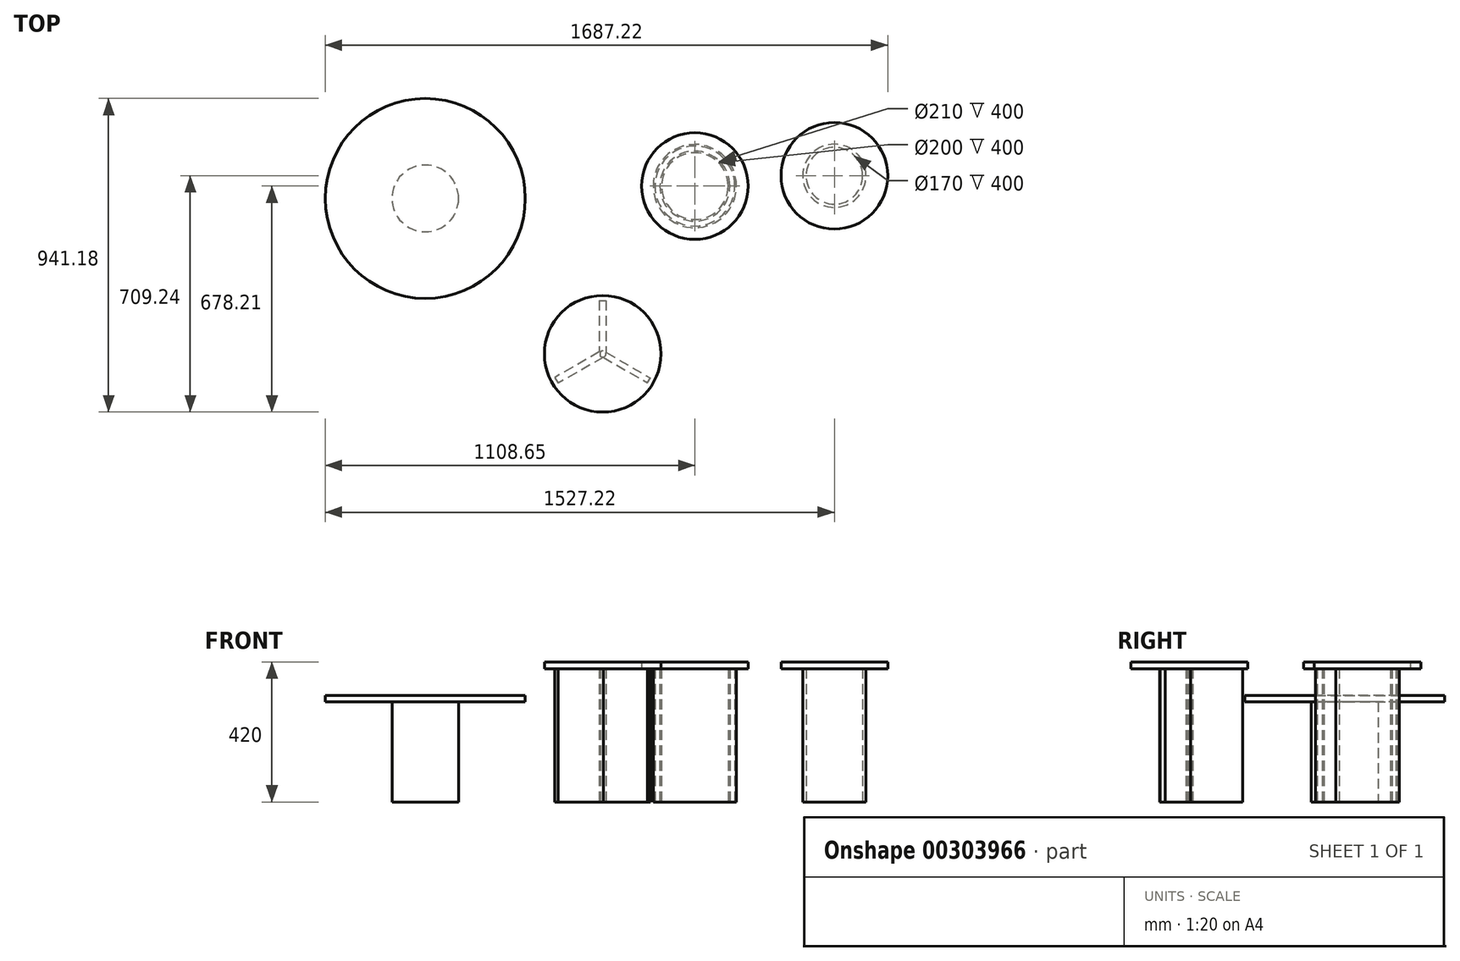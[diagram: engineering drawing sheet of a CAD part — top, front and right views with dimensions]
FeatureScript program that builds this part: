
annotation { "Feature Type Name" : "Feature", "Feature Type Description" : "" }
export const myFeature = defineFeature(function(context is Context, id is Id, definition is map)
    precondition{}
    {
        {
            var Q0;
            Q0=qCreatedBy(makeId("Top.planeOp"),FACE);
            var sketch = newSketch(context, id + "F0", { "sketchPlane" : qUnion([Q0])});
            skCircle(sketch, "E0", {"center": v(0, 0) * mm, "radius": 125 * mm});
            skCircle(sketch, "E1", {"center": v(0, 0) * mm, "radius": 100 * mm});
            skSolve(sketch);
        }
        {
            var Q0;
            Q0 = qSketchRegion(id + "F0", true);
            extrude(context, id + "F1", {"entities" : qUnion([Q0]), "depth" : 400 * mm});
        }
        {
            var Q0;
            Q0=qCreatedBy(makeId("Top.planeOp"),FACE);
            var sketch = newSketch(context, id + "F2", { "sketchPlane" : qUnion([Q0])});
            skCircle(sketch, "E2.0", {"center": v(0, 0) * mm, "radius": 125 * mm, "construction": true});
            skCircle(sketch, "E2.1", {"center": v(0, 0) * mm, "radius": 100 * mm, "construction": true});
            skCircle(sketch, "E3", {"center": v(0, 0) * mm, "radius": 120 * mm});
            skCircle(sketch, "E4", {"center": v(0, 0) * mm, "radius": 105 * mm});
            skSolve(sketch);
        }
        {
            var Q0;
            Q0 = qSketchRegion(id + "F2", true);
            var Q1;
            Q1=makeQuery(id+"F1.opExtrude","CAP_FACE",FACE,{"disambiguationData":[OSD([sQuery(id+"F0.wireOp",EDGE,"E0"),sQuery(id+"F0.wireOp",EDGE,"E1")])],"isStart":false});
            extrude(context, id + "F3", {"entities" : qUnion([Q0]), "endBound" : BoundingType.UP_TO_SURFACE, "endBoundEntityFace" : qUnion([Q1]), "depth" : 25 * mm});
        }
        {
            var Q0;
            Q0=makeQuery(id+"F1.opExtrude","CAP_FACE",FACE,{"disambiguationData":[OSD([sQuery(id+"F0.wireOp",EDGE,"E0"),sQuery(id+"F0.wireOp",EDGE,"E1")])],"isStart":false});
            var sketch = newSketch(context, id + "F4", { "sketchPlane" : qUnion([Q0])});
            skCircle(sketch, "E5", {"center": v(0, 0) * mm, "radius": 160 * mm});
            skSolve(sketch);
        }
        {
            var Q0;
            Q0 = qSketchRegion(id + "F4", true);
            extrude(context, id + "F5", {"entities" : qUnion([Q0]), "depth" : 20 * mm});
        }
        {
            var Q0;
            Q0=qCreatedBy(makeId("Top.planeOp"),FACE);
            var sketch = newSketch(context, id + "F6", { "sketchPlane" : qUnion([Q0])});
            skCircle(sketch, "E6", {"center": v(418.57, 31.03) * mm, "radius": 95 * mm});
            skCircle(sketch, "E7", {"center": v(418.57, 31.03) * mm, "radius": 85 * mm});
            skSolve(sketch);
        }
        {
            var Q0;
            Q0 = qSketchRegion(id + "F6", true);
            extrude(context, id + "F7", {"entities" : qUnion([Q0]), "depth" : 400 * mm});
        }
        {
            var Q0;
            Q0=makeQuery(id+"F7.opExtrude","CAP_FACE",FACE,{"disambiguationData":[OSD([sQuery(id+"F6.wireOp",EDGE,"E6"),sQuery(id+"F6.wireOp",EDGE,"E7")])],"isStart":false});
            var sketch = newSketch(context, id + "F8", { "sketchPlane" : qUnion([Q0])});
            skCircle(sketch, "E8", {"center": v(418.57, 31.03) * mm, "radius": 160 * mm});
            skSolve(sketch);
        }
        {
            var Q0;
            Q0 = qSketchRegion(id + "F8", true);
            extrude(context, id + "F9", {"entities" : qUnion([Q0]), "depth" : 20 * mm});
        }
        {
            var Q0;
            Q0=qCreatedBy(makeId("Top.planeOp"),FACE);
            var sketch = newSketch(context, id + "F10", { "sketchPlane" : qUnion([Q0])});
            skCircle(sketch, "E9", {"center": v(-808.65, -37.03) * mm, "radius": 100 * mm});
            skSolve(sketch);
        }
        {
            var Q0;
            Q0=makeQuery(id+"F10.imprint","IMPRINT",FACE,{"disambiguationData":[TD([[makeQuery(id+"F10.imprint","IMPRINT",EDGE,{"derivedFrom":sQuery(id+"F10.wireOp",EDGE,"E9")}),1.0]])]});
            extrude(context, id + "F11", {"entities" : qUnion([Q0]), "depth" : 300 * mm});
        }
        {
            var Q0;
            Q0=makeQuery(id+"F11.opExtrude","CAP_FACE",FACE,{"disambiguationData":[OSD([sQuery(id+"F10.wireOp",EDGE,"E9")])],"isStart":false});
            var sketch = newSketch(context, id + "F12", { "sketchPlane" : qUnion([Q0])});
            skCircle(sketch, "E10", {"center": v(-808.65, -37.03) * mm, "radius": 300 * mm});
            skSolve(sketch);
        }
        {
            var Q0;
            Q0 = qSketchRegion(id + "F12", true);
            extrude(context, id + "F13", {"entities" : qUnion([Q0]), "operationType" : NewBodyOperationType.ADD, "depth" : 20 * mm});
        }
        {
            var Q0;
            Q0=qCreatedBy(makeId("Top.planeOp"),FACE);
            var sketch = newSketch(context, id + "F14", { "sketchPlane" : qUnion([Q0])});
            skLineSegment(sketch, "E11", {"start": v(-276.38, -303.2) * mm, "end": v(-276.38, -503.2) * mm});
            skLineSegment(sketch, "E12", {"start": v(-276.38, -503.2) * mm, "end": v(-449.59, -603.2) * mm});
            skLineSegment(sketch, "E13", {"start": v(-276.38, -503.2) * mm, "end": v(-103.18, -603.2) * mm});
            skArc(sketch, "E14.0.endCap", {"start": v(-266.38, -503.2) * mm, "mid": v(-276.38, -513.2) * mm, "end": v(-286.38, -503.2) * mm});
            skLineSegment(sketch, "E14.0.left", {"start": v(-266.38, -343.2) * mm, "end": v(-266.38, -503.2) * mm});
            skLineSegment(sketch, "E14.0.right", {"start": v(-286.38, -343.2) * mm, "end": v(-286.38, -503.2) * mm});
            skArc(sketch, "E14.1.startCap", {"start": v(-280.65, -510.6) * mm, "mid": v(-283.77, -498.94) * mm, "end": v(-272.12, -495.82) * mm});
            skLineSegment(sketch, "E14.1.left", {"start": v(-272.12, -495.82) * mm, "end": v(-133.55, -575.82) * mm});
            skLineSegment(sketch, "E14.1.right", {"start": v(-280.65, -510.6) * mm, "end": v(-142.08, -590.6) * mm});
            skArc(sketch, "E14.2.startCap", {"start": v(-281.38, -494.55) * mm, "mid": v(-267.72, -498.2) * mm, "end": v(-271.38, -511.87) * mm});
            skLineSegment(sketch, "E14.2.left", {"start": v(-271.38, -511.87) * mm, "end": v(-409.95, -591.87) * mm});
            skLineSegment(sketch, "E14.2.right", {"start": v(-281.38, -494.55) * mm, "end": v(-419.95, -574.55) * mm});
            skLineSegment(sketch, "E15", {"start": v(-286.38, -343.2) * mm, "end": v(-266.38, -343.2) * mm});
            skLineSegment(sketch, "E16", {"start": v(-419.95, -574.55) * mm, "end": v(-409.95, -591.87) * mm});
            skLineSegment(sketch, "E17", {"start": v(-142.08, -590.6) * mm, "end": v(-133.55, -575.82) * mm});
            skSolve(sketch);
        }
        {
            var Q0;
            Q0 = qSketchRegion(id + "F14", true);
            extrude(context, id + "F15", {"entities" : qUnion([Q0]), "depth" : 400 * mm});
        }
        {
            var Q0;
            Q0=makeQuery(id+"F15.opExtrude","CAP_FACE",FACE,{"disambiguationData":[OSD([sQuery(id+"F14.wireOp",EDGE,"E14.0.endCap"),sQuery(id+"F14.wireOp",EDGE,"E14.0.left"),sQuery(id+"F14.wireOp",EDGE,"E14.0.right"),sQuery(id+"F14.wireOp",EDGE,"E14.1.startCap"),sQuery(id+"F14.wireOp",EDGE,"E14.1.left"),sQuery(id+"F14.wireOp",EDGE,"E14.1.right"),sQuery(id+"F14.wireOp",EDGE,"E14.2.startCap"),sQuery(id+"F14.wireOp",EDGE,"E14.2.left"),sQuery(id+"F14.wireOp",EDGE,"E14.2.right"),sQuery(id+"F14.wireOp",EDGE,"E15"),sQuery(id+"F14.wireOp",EDGE,"E16"),sQuery(id+"F14.wireOp",EDGE,"E17")])],"isStart":false});
            var sketch = newSketch(context, id + "F16", { "sketchPlane" : qUnion([Q0])});
            skCircle(sketch, "E18", {"center": v(-276.38, -503.2) * mm, "radius": 175 * mm});
            skSolve(sketch);
        }
        {
            var Q0;
            Q0 = qSketchRegion(id + "F16", true);
            extrude(context, id + "F17", {"entities" : qUnion([Q0]), "operationType" : NewBodyOperationType.ADD, "depth" : 20 * mm});
        }
    });
